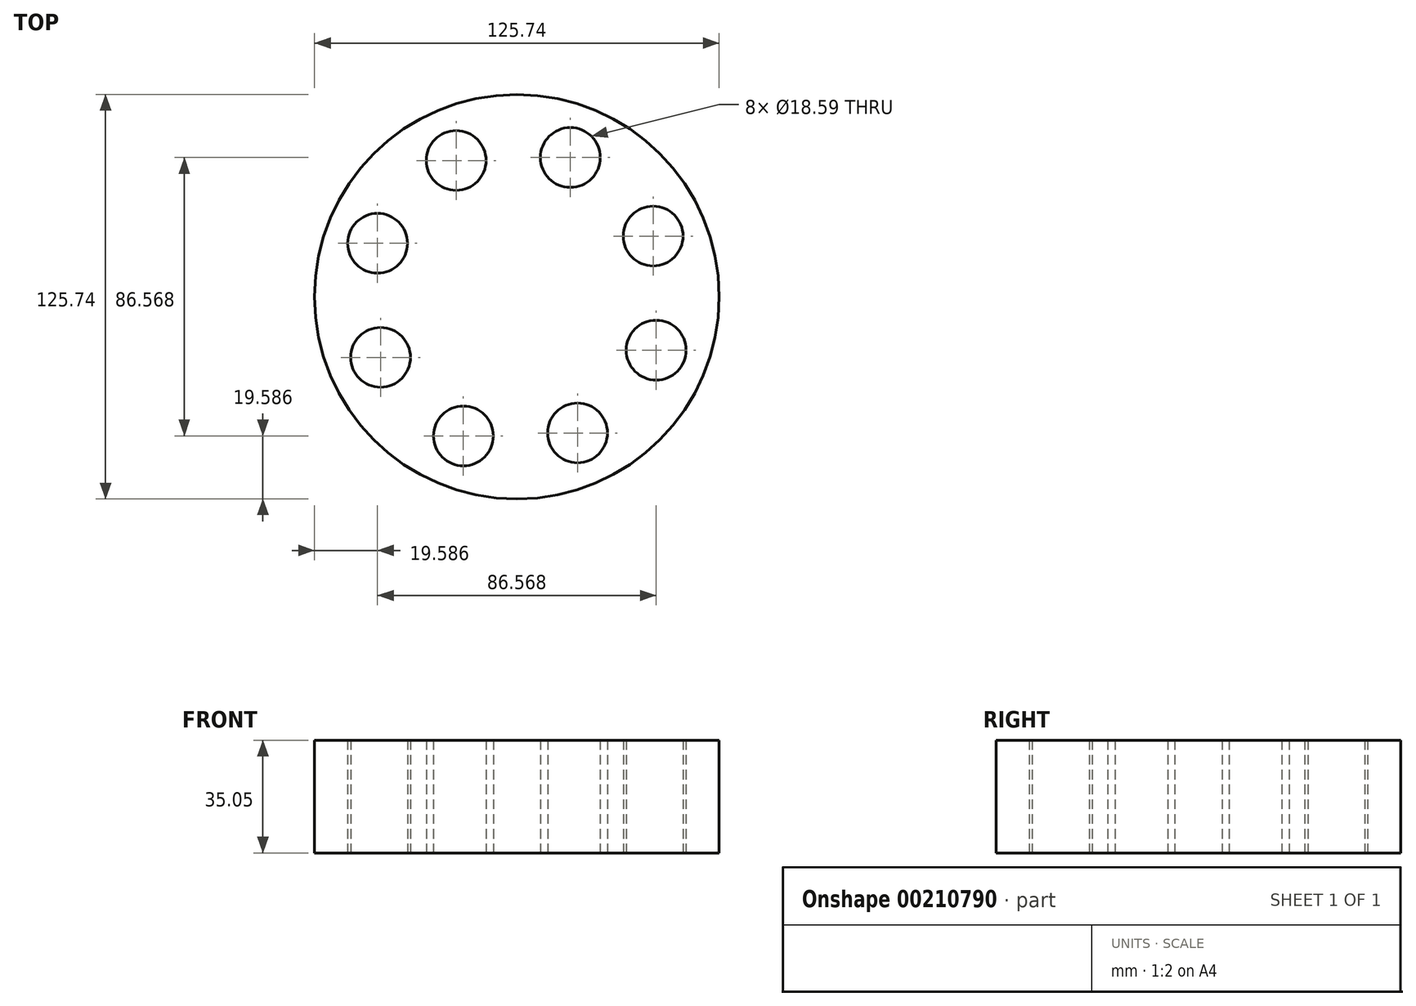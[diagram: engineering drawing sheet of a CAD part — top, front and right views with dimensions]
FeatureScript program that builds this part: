
annotation { "Feature Type Name" : "Feature", "Feature Type Description" : "" }
export const myFeature = defineFeature(function(context is Context, id is Id, definition is map)
    precondition{}
    {
        {
            var Q0;
            Q0=qCreatedBy(makeId("Top.planeOp"),FACE);
            var sketch = newSketch(context, id + "F0", { "sketchPlane" : qUnion([Q0])});
            skCircle(sketch, "E0", {"center": v(0, 0) * mm, "radius": 62.87 * mm});
            skCircle(sketch, "E1", {"center": v(-16.61, -43.28) * mm, "radius": 9.3 * mm});
            skCircle(sketch, "E2.1.0", {"center": v(18.86, -42.35) * mm, "radius": 9.3 * mm});
            skCircle(sketch, "E2.2.0", {"center": v(43.28, -16.61) * mm, "radius": 9.3 * mm});
            skCircle(sketch, "E2.3.0", {"center": v(42.35, 18.86) * mm, "radius": 9.3 * mm});
            skCircle(sketch, "E2.4.0", {"center": v(16.61, 43.28) * mm, "radius": 9.3 * mm});
            skCircle(sketch, "E2.5.0", {"center": v(-18.86, 42.35) * mm, "radius": 9.3 * mm});
            skCircle(sketch, "E2.6.0", {"center": v(-43.28, 16.61) * mm, "radius": 9.3 * mm});
            skCircle(sketch, "E2.7.0", {"center": v(-42.35, -18.86) * mm, "radius": 9.3 * mm});
            skSolve(sketch);
        }
        {
            var Q0;
            Q0=makeQuery(id+"F0.imprint","IMPRINT",FACE,{"disambiguationData":[TD([[makeQuery(id+"F0.imprint","IMPRINT",EDGE,{"derivedFrom":sQuery(id+"F0.wireOp",EDGE,"E0")}),1.0]])]});
            extrude(context, id + "F1", {"entities" : qUnion([Q0]), "depth" : 9.65 * mm});
        }
        {
            var Q0;
            Q0=makeQuery(id+"F1.opExtrude","CAP_FACE",FACE,{"disambiguationData":[OSD([sQuery(id+"F0.wireOp",EDGE,"E0"),sQuery(id+"F0.wireOp",EDGE,"E1"),sQuery(id+"F0.wireOp",EDGE,"E2.1.0"),sQuery(id+"F0.wireOp",EDGE,"E2.2.0"),sQuery(id+"F0.wireOp",EDGE,"E2.3.0"),sQuery(id+"F0.wireOp",EDGE,"E2.4.0"),sQuery(id+"F0.wireOp",EDGE,"E2.5.0"),sQuery(id+"F0.wireOp",EDGE,"E2.6.0"),sQuery(id+"F0.wireOp",EDGE,"E2.7.0")])],"isStart":false});
            extrude(context, id + "F2", {"entities" : qUnion([Q0]), "operationType" : NewBodyOperationType.ADD, "depth" : 25.4 * mm});
        }
    });
